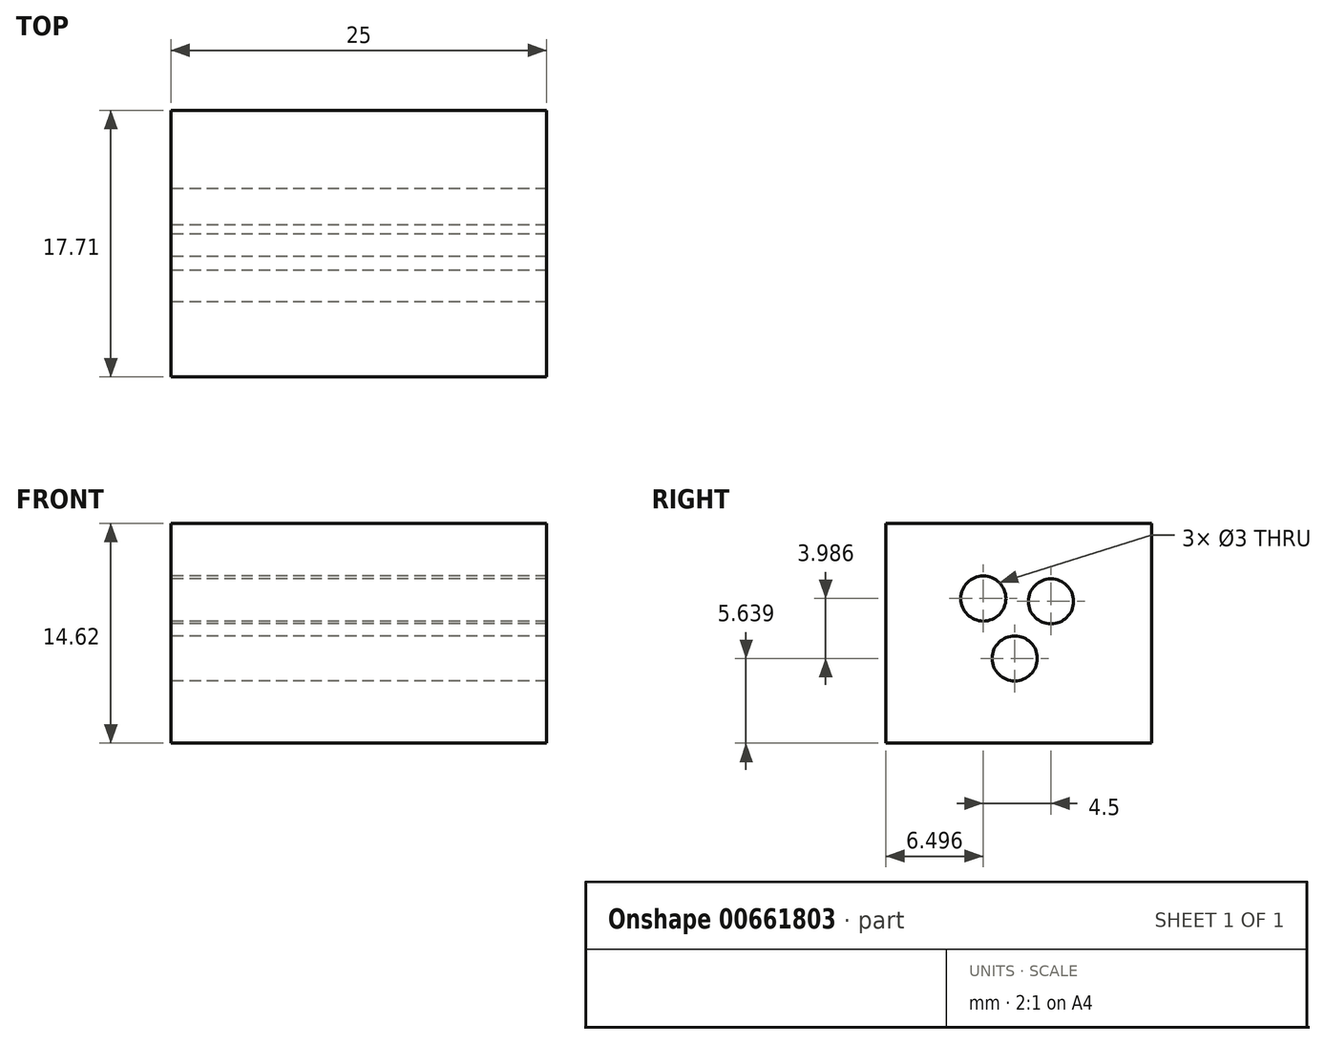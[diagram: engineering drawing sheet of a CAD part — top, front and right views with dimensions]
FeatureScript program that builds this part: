
annotation { "Feature Type Name" : "Feature", "Feature Type Description" : "" }
export const myFeature = defineFeature(function(context is Context, id is Id, definition is map)
    precondition{}
    {
        {
            var Q0;
            Q0=qCreatedBy(makeId("Right.planeOp"),FACE);
            var sketch = newSketch(context, id + "F0", { "sketchPlane" : qUnion([Q0])});
            skCircle(sketch, "E0", {"center": v(-24.68, 30.58) * mm, "radius": 1.5 * mm});
            skCircle(sketch, "E1", {"center": v(-20.18, 30.4) * mm, "radius": 1.5 * mm});
            skCircle(sketch, "E2", {"center": v(-22.6, 26.6) * mm, "radius": 1.5 * mm});
            skLineSegment(sketch, "E3", {"start": v(-31.18, 35.58) * mm, "end": v(-13.47, 35.58) * mm});
            skLineSegment(sketch, "E4", {"start": v(-31.18, 35.58) * mm, "end": v(-31.18, 20.96) * mm});
            skLineSegment(sketch, "E5", {"start": v(-31.18, 20.96) * mm, "end": v(-13.47, 20.96) * mm});
            skLineSegment(sketch, "E6", {"start": v(-13.47, 20.96) * mm, "end": v(-31.18, 20.96) * mm});
            skLineSegment(sketch, "E7", {"start": v(-13.47, 35.58) * mm, "end": v(-13.47, 20.96) * mm});
            skSolve(sketch);
        }
        {
            var Q0;
            Q0 = qSketchRegion(id + "F0", true);
            var Q1;
            Q1=makeQuery(id+"F0.imprint","IMPRINT",FACE,{"disambiguationData":[TD([[makeQuery(id+"F0.imprint","IMPRINT",EDGE,{"derivedFrom":sQuery(id+"F0.wireOp",EDGE,"E0")}),-1.0]])]});
            extrude(context, id + "F1", {"entities" : qUnion([Q0, Q1]), "depth" : 25 * mm, "offsetDistance" : 25 * mm});
        }
    });
